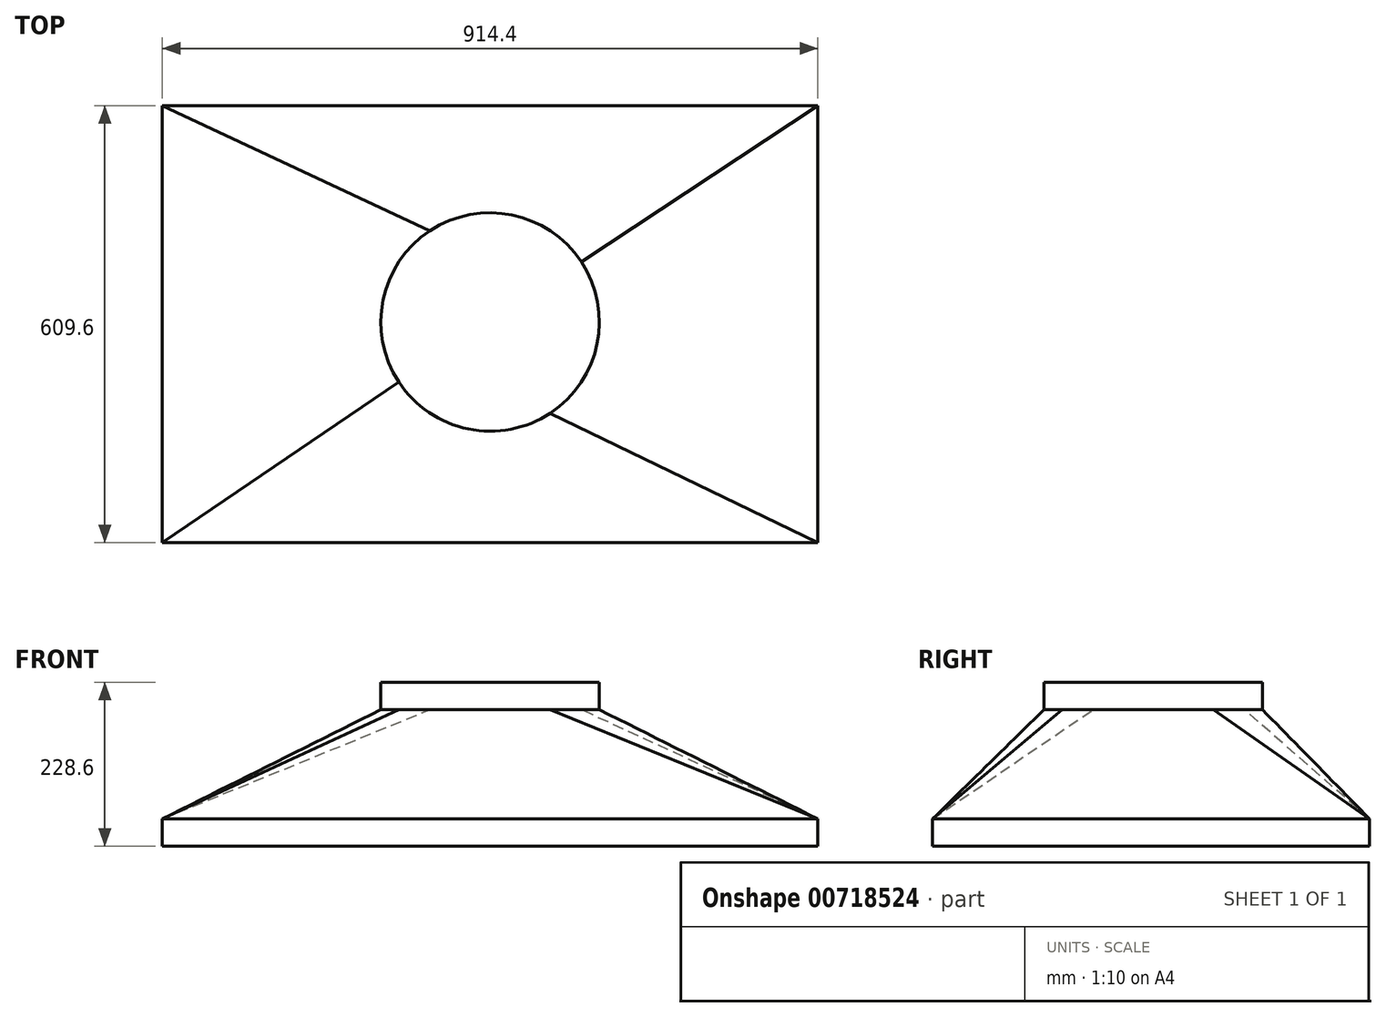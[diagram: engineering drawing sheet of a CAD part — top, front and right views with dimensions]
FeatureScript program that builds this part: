
annotation { "Feature Type Name" : "Feature", "Feature Type Description" : "" }
export const myFeature = defineFeature(function(context is Context, id is Id, definition is map)
    precondition{}
    {
        {
            var Q0;
            Q0=qCreatedBy(makeId("Top.planeOp"),FACE);
            var sketch = newSketch(context, id + "F0", { "sketchPlane" : qUnion([Q0])});
            skLineSegment(sketch, "E0.bottom", {"start": v(457.2, 301.77) * mm, "end": v(-457.2, 301.77) * mm});
            skLineSegment(sketch, "E0.top", {"start": v(457.2, -307.83) * mm, "end": v(-457.2, -307.83) * mm});
            skLineSegment(sketch, "E0.left", {"start": v(457.2, 301.77) * mm, "end": v(457.2, -307.83) * mm});
            skLineSegment(sketch, "E0.right", {"start": v(-457.2, 301.77) * mm, "end": v(-457.2, -307.83) * mm});
            skPoint(sketch, "E0.middle", {"position": v(0, -3.03) * mm});
            skSolve(sketch);
        }
        {
            var Q0;
            Q0=makeQuery(id+"F0.imprint","IMPRINT",FACE,{"disambiguationData":[TD([[makeQuery(id+"F0.imprint","IMPRINT",EDGE,{"derivedFrom":sQuery(id+"F0.wireOp",EDGE,"E0.bottom")}),1.0]])]});
            extrude(context, id + "F1", {"entities" : qUnion([Q0]), "depth" : 38.1 * mm, "offsetDistance" : 25.4 * mm});
        }
        {
            var Q0;
            Q0=makeQuery(id+"F1.opExtrude","CAP_FACE",FACE,{"disambiguationData":[OSD([sQuery(id+"F0.wireOp",EDGE,"E0.bottom"),sQuery(id+"F0.wireOp",EDGE,"E0.top"),sQuery(id+"F0.wireOp",EDGE,"E0.left"),sQuery(id+"F0.wireOp",EDGE,"E0.right")])],"isStart":false});
            cPlane(context, id + "F2", {"entities" : qUnion([Q0]), "cplaneType" : CPlaneType.OFFSET, "offset" : 152.4 * mm, "width" : 152.4 * mm, "height" : 152.4 * mm});
        }
        {
            var Q0;
            Q0=qCreatedBy(id+"F2.planeOp",FACE);
            var sketch = newSketch(context, id + "F3", { "sketchPlane" : qUnion([Q0])});
            skCircle(sketch, "E1", {"center": v(0, 0) * mm, "radius": 152.4 * mm});
            skSolve(sketch);
        }
        {
            var Q1;
            Q1=makeQuery(id+"F1.opExtrude","CAP_FACE",FACE,{"disambiguationData":[OSD([sQuery(id+"F0.wireOp",EDGE,"E0.bottom"),sQuery(id+"F0.wireOp",EDGE,"E0.top"),sQuery(id+"F0.wireOp",EDGE,"E0.left"),sQuery(id+"F0.wireOp",EDGE,"E0.right")])],"isStart":false});
            var Q2;
            Q2=makeQuery(id+"F3.imprint","IMPRINT",FACE,{"disambiguationData":[TD([[makeQuery(id+"F3.imprint","IMPRINT",EDGE,{"derivedFrom":sQuery(id+"F3.wireOp",EDGE,"E1")}),1.0]])]});
            loft(context, id + "F4", {"operationType" : NewBodyOperationType.ADD, "sheetProfilesArray" : [{ "sheetProfileEntities" : qUnion([Q1]) }, { "sheetProfileEntities" : qUnion([Q2]) }]});
        }
        {
            var Q0;
            Q0=makeQuery(id+"F4.opLoft","CAP_FACE",FACE,{"disambiguationData":[OSD([makeQuery(id+"F3.imprint","IMPRINT",FACE,{"disambiguationData":[TD([[makeQuery(id+"F3.imprint","IMPRINT",EDGE,{"derivedFrom":sQuery(id+"F3.wireOp",EDGE,"E1")}),1.0]])]})])],"isStart":true});
            extrude(context, id + "F5", {"entities" : qUnion([Q0]), "operationType" : NewBodyOperationType.ADD, "depth" : 38.1 * mm, "offsetDistance" : 25.4 * mm});
        }
    });
